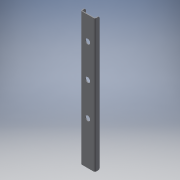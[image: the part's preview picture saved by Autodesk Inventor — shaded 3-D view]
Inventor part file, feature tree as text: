
AUTODESK INVENTOR PART (.ipt)
format: ipt  version: 2016 (Build 200138000, 138)  size: 154,112 bytes
history: native  units: mm
features: sheet_metal_op x2, sketch x2, extrude x1, pattern_linear x1, chamfer x1, other x1
ambient origin geometry x8: Origin, YZ Plane, XZ Plane, XY Plane, X Axis, Y Axis, Z Axis, Center Point
bodies: Solid1 (feature_tree)
feature tree (8):
  sheet_metal_op  "Contour Flange1"
  extrude  "Extrusion1"  Depth=50.0mm
  pattern_linear  "Rectangular Pattern1"  Spacing1=3.0mm  [1 undecoded]
  chamfer  "Corner Round1"
  sketch  "Sketch1"  dims[d0=15.0mm d1=50.0mm]
  other  "Plate1"
  sheet_metal_op  "Bend1"
  sketch  "Sketch2"  dims[d2=15.0mm d3=3.0mm d4=1.5mm d5=6.0mm d6=3.0mm d8=3.0mm d9=0.5mm d10=12.0mm d11=3.0mm d12=3.0mm d13=90.0mm d15=22.0mm d16=10.0mm d17=0.0mm d21=6.0mm]
note: 1 required parameter value undecoded (feature->parameter linkage not recoverable at this tier; creation-order binding heuristic only, values carry confidence <= 0.55)
